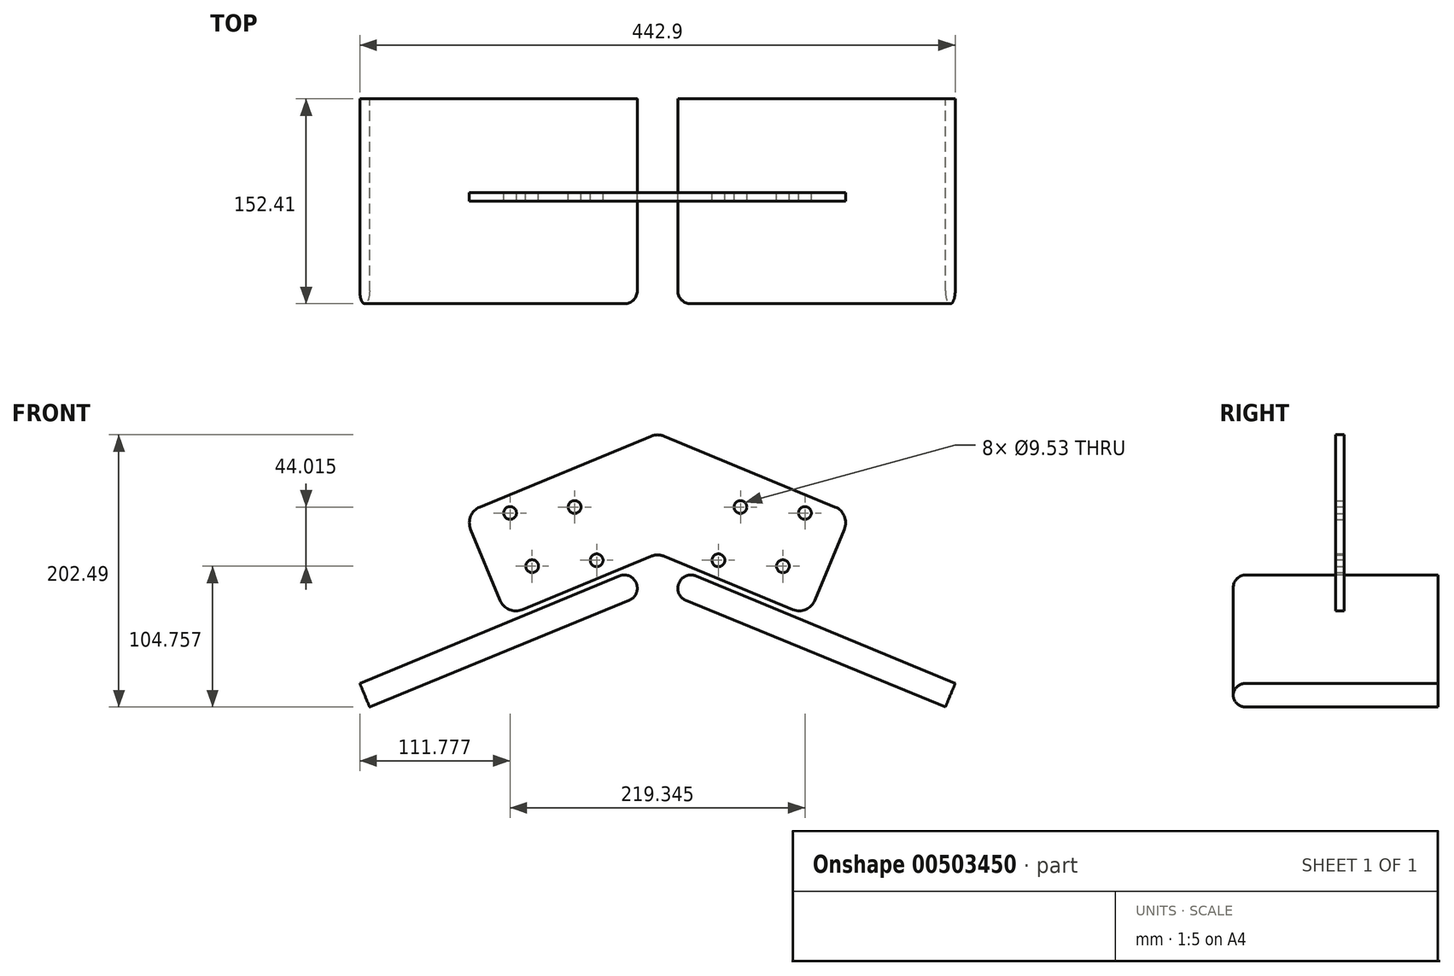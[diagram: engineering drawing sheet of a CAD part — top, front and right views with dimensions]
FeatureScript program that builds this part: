
annotation { "Feature Type Name" : "Feature", "Feature Type Description" : "" }
export const myFeature = defineFeature(function(context is Context, id is Id, definition is map)
    precondition{}
    {
        {
            var Q0;
            Q0=qCreatedBy(makeId("Front.planeOp"),FACE);
            var sketch = newSketch(context, id + "F0", { "sketchPlane" : qUnion([Q0])});
            skLineSegment(sketch, "E0", {"start": v(0, 0) * mm, "end": v(-112.28, -46.5) * mm});
            skLineSegment(sketch, "E1", {"start": v(0, 0) * mm, "end": v(0, 89.35) * mm});
            skLineSegment(sketch, "E2", {"start": v(-112.28, -46.5) * mm, "end": v(-143.87, 29.76) * mm});
            skLineSegment(sketch, "E3", {"start": v(-143.87, 29.76) * mm, "end": v(0, 89.35) * mm});
            skPoint(sketch, "E4", {"position": v(-15.88, -22.04) * mm});
            skLineSegment(sketch, "E5.MirrorCS", {"start": v(0, 0) * mm, "end": v(112.28, -46.5) * mm});
            skPoint(sketch, "E6.MirrorP", {"position": v(15.88, -22.04) * mm});
            skLineSegment(sketch, "E7.MirrorCS", {"start": v(112.28, -46.5) * mm, "end": v(143.87, 29.76) * mm});
            skLineSegment(sketch, "E8.MirrorCS", {"start": v(143.87, 29.76) * mm, "end": v(0, 89.35) * mm});
            skPoint(sketch, "E9.MirrorP", {"position": v(15.88, 98.24) * mm});
            skLineSegment(sketch, "E10", {"start": v(-15.88, -22.04) * mm, "end": v(-45.04, 48.36) * mm, "construction": true});
            skLineSegment(sketch, "E11", {"start": v(-15.88, 98.24) * mm, "end": v(13.29, 27.84) * mm, "construction": true});
            skCircle(sketch, "E12", {"center": v(-93.27, -9.42) * mm, "radius": 4.76 * mm});
            skLineSegment(sketch, "E13", {"start": v(-93.27, -9.42) * mm, "end": v(-114.53, 41.91) * mm, "construction": true});
            skCircle(sketch, "E14", {"center": v(-109.67, 30.18) * mm, "radius": 4.76 * mm});
            skCircle(sketch, "E15.MirrorC", {"center": v(93.27, -9.42) * mm, "radius": 4.76 * mm});
            skCircle(sketch, "E16.MirrorC", {"center": v(109.67, 30.18) * mm, "radius": 4.76 * mm});
            skCircle(sketch, "E17", {"center": v(-61.68, 34.6) * mm, "radius": 4.76 * mm});
            skLineSegment(sketch, "E18", {"start": v(-61.68, 34.6) * mm, "end": v(-40.42, -16.74) * mm});
            skCircle(sketch, "E19", {"center": v(-45.28, -5) * mm, "radius": 4.76 * mm});
            skCircle(sketch, "E20.MirrorC", {"center": v(45.28, -5) * mm, "radius": 4.76 * mm});
            skCircle(sketch, "E21.MirrorC", {"center": v(61.68, 34.6) * mm, "radius": 4.76 * mm});
            skPoint(sketch, "E22", {"position": v(-103.9, 16.24) * mm});
            skLineSegment(sketch, "E23", {"start": v(-15.88, -22.04) * mm, "end": v(-19.63, -12.97) * mm});
            skLineSegment(sketch, "E24", {"start": v(-19.63, -12.97) * mm, "end": v(-221.45, -96.57) * mm});
            skLineSegment(sketch, "E25", {"start": v(-221.45, -96.57) * mm, "end": v(-217.8, -105.37) * mm});
            skLineSegment(sketch, "E26", {"start": v(-217.8, -105.37) * mm, "end": v(-15.88, -22.04) * mm, "construction": true});
            skLineSegment(sketch, "E27.MirrorCS", {"start": v(-214.19, -114.18) * mm, "end": v(-217.8, -105.37) * mm});
            skLineSegment(sketch, "E28.MirrorCS", {"start": v(-12.14, -31.12) * mm, "end": v(-214.19, -114.18) * mm});
            skLineSegment(sketch, "E29.MirrorCS", {"start": v(-15.87, -22.04) * mm, "end": v(-45.04, 48.36) * mm, "construction": true});
            skLineSegment(sketch, "E30", {"start": v(-19.63, -12.97) * mm, "end": v(-12.14, -31.12) * mm});
            skLineSegment(sketch, "E31.MirrorCS", {"start": v(19.63, -12.97) * mm, "end": v(12.14, -31.12) * mm});
            skLineSegment(sketch, "E32.MirrorCS", {"start": v(19.63, -12.97) * mm, "end": v(221.45, -96.57) * mm});
            skLineSegment(sketch, "E33.MirrorCS", {"start": v(12.14, -31.12) * mm, "end": v(214.19, -114.18) * mm});
            skLineSegment(sketch, "E34.MirrorCS", {"start": v(221.45, -96.57) * mm, "end": v(217.8, -105.37) * mm});
            skLineSegment(sketch, "E35.MirrorCS", {"start": v(214.19, -114.18) * mm, "end": v(217.8, -105.37) * mm});
            skSolve(sketch);
        }
        {
            var Q0;
            Q0=qSketchRegion(id+"F0",true);
            extrude(context, id + "F1", {"entities" : qUnion([Q0]), "depth" : 6.35 * mm, "offsetDistance" : 25.4 * mm, "symmetric" : true});
        }
        {
            var Q0;
            Q0=makeQuery(id+"F1.opExtrude","SWEPT_EDGE",EDGE,{"disambiguationData":[OSD([sQuery(id+"F0.wireOp",EDGE,"E2"),sQuery(id+"F0.wireOp",EDGE,"E3")])]});
            var Q1;
            Q1=makeQuery(id+"F1.opExtrude","SWEPT_EDGE",EDGE,{"disambiguationData":[OSD([sQuery(id+"F0.wireOp",EDGE,"E3"),sQuery(id+"F0.wireOp",EDGE,"E1"),sQuery(id+"F0.wireOp",EDGE,"E8.MirrorCS")])]});
            var Q2;
            Q2=makeQuery(id+"F1.opExtrude","SWEPT_EDGE",EDGE,{"disambiguationData":[OSD([sQuery(id+"F0.wireOp",EDGE,"E0"),sQuery(id+"F0.wireOp",EDGE,"E5.MirrorCS"),sQuery(id+"F0.wireOp",EDGE,"E1")])]});
            var Q3;
            Q3=makeQuery(id+"F1.opExtrude","SWEPT_EDGE",EDGE,{"disambiguationData":[OSD([sQuery(id+"F0.wireOp",EDGE,"E5.MirrorCS"),sQuery(id+"F0.wireOp",EDGE,"E7.MirrorCS")])]});
            var Q4;
            Q4=makeQuery(id+"F1.opExtrude","SWEPT_EDGE",EDGE,{"disambiguationData":[OSD([sQuery(id+"F0.wireOp",EDGE,"E7.MirrorCS"),sQuery(id+"F0.wireOp",EDGE,"E8.MirrorCS")])]});
            var Q5;
            Q5=makeQuery(id+"F1.opExtrude","SWEPT_EDGE",EDGE,{"disambiguationData":[OSD([sQuery(id+"F0.wireOp",EDGE,"E0"),sQuery(id+"F0.wireOp",EDGE,"E2")])]});
            fillet(context, id + "F2", {"entities" : qUnion([Q0, Q1, Q2, Q3, Q4, Q5]), "radius" : 12.7 * mm, "tangentPropagation" : true, "allowEdgeOverflow" : false});
        }
        {
            var Q0;
            Q0=makeQuery(id+"F1.opExtrude","CAP_FACE",FACE,{"disambiguationData":[OSD([sQuery(id+"F0.wireOp",EDGE,"E24"),sQuery(id+"F0.wireOp",EDGE,"E25"),sQuery(id+"F0.wireOp",EDGE,"E27.MirrorCS"),sQuery(id+"F0.wireOp",EDGE,"E28.MirrorCS"),sQuery(id+"F0.wireOp",EDGE,"E30")])],"isStart":false});
            var Q1;
            Q1=makeQuery(id+"F1.opExtrude","CAP_FACE",FACE,{"disambiguationData":[OSD([sQuery(id+"F0.wireOp",EDGE,"E31.MirrorCS"),sQuery(id+"F0.wireOp",EDGE,"E32.MirrorCS"),sQuery(id+"F0.wireOp",EDGE,"E33.MirrorCS"),sQuery(id+"F0.wireOp",EDGE,"E34.MirrorCS"),sQuery(id+"F0.wireOp",EDGE,"E35.MirrorCS")])],"isStart":false});
            extrude(context, id + "F3", {"entities" : qUnion([Q0, Q1]), "operationType" : NewBodyOperationType.ADD, "depth" : 152.4 * mm, "offsetDistance" : 25.4 * mm, "symmetric" : true});
        }
        {
            var Q0;
            Q0=makeQuery(id+"F3.opExtrude","SWEPT_EDGE",EDGE,{"disambiguationData":[OSD([sQuery(id+"F0.wireOp",EDGE,"E31.MirrorCS"),sQuery(id+"F0.wireOp",EDGE,"E32.MirrorCS")])]});
            var Q1;
            Q1=makeQuery(id+"F3.opExtrude","SWEPT_EDGE",EDGE,{"disambiguationData":[OSD([sQuery(id+"F0.wireOp",EDGE,"E31.MirrorCS"),sQuery(id+"F0.wireOp",EDGE,"E33.MirrorCS")])]});
            var Q2;
            Q2=makeQuery(id+"F3.opExtrude","CAP_EDGE",EDGE,{"disambiguationData":[OSD([sQuery(id+"F0.wireOp",EDGE,"E32.MirrorCS")])],"isStart":false});
            var Q3;
            Q3=makeQuery(id+"F3.opExtrude","CAP_EDGE",EDGE,{"disambiguationData":[OSD([sQuery(id+"F0.wireOp",EDGE,"E33.MirrorCS")])],"isStart":false});
            var Q4;
            Q4=makeQuery(id+"F3.opExtrude","SWEPT_EDGE",EDGE,{"disambiguationData":[OSD([sQuery(id+"F0.wireOp",EDGE,"E28.MirrorCS"),sQuery(id+"F0.wireOp",EDGE,"E30")])]});
            var Q5;
            Q5=makeQuery(id+"F3.opExtrude","CAP_EDGE",EDGE,{"disambiguationData":[OSD([sQuery(id+"F0.wireOp",EDGE,"E24")])],"isStart":false});
            var Q6;
            Q6=makeQuery(id+"F3.opExtrude","CAP_EDGE",EDGE,{"disambiguationData":[OSD([sQuery(id+"F0.wireOp",EDGE,"E28.MirrorCS")])],"isStart":false});
            var Q7;
            Q7=makeQuery(id+"F3.opExtrude","SWEPT_EDGE",EDGE,{"disambiguationData":[OSD([sQuery(id+"F0.wireOp",EDGE,"E24"),sQuery(id+"F0.wireOp",EDGE,"E30")])]});
            var Q8;
            Q8=makeQuery(id+"F3.opExtrude","CAP_EDGE",EDGE,{"disambiguationData":[OSD([sQuery(id+"F0.wireOp",EDGE,"E30")])],"isStart":false});
            var Q9;
            Q9=makeQuery(id+"F3.opExtrude","CAP_EDGE",EDGE,{"disambiguationData":[OSD([sQuery(id+"F0.wireOp",EDGE,"E31.MirrorCS")])],"isStart":false});
            fillet(context, id + "F4", {"entities" : qUnion([Q0, Q1, Q2, Q3, Q4, Q5, Q6, Q7, Q8, Q9]), "radius" : 9.52 * mm, "tangentPropagation" : true, "allowEdgeOverflow" : false});
        }
    });
